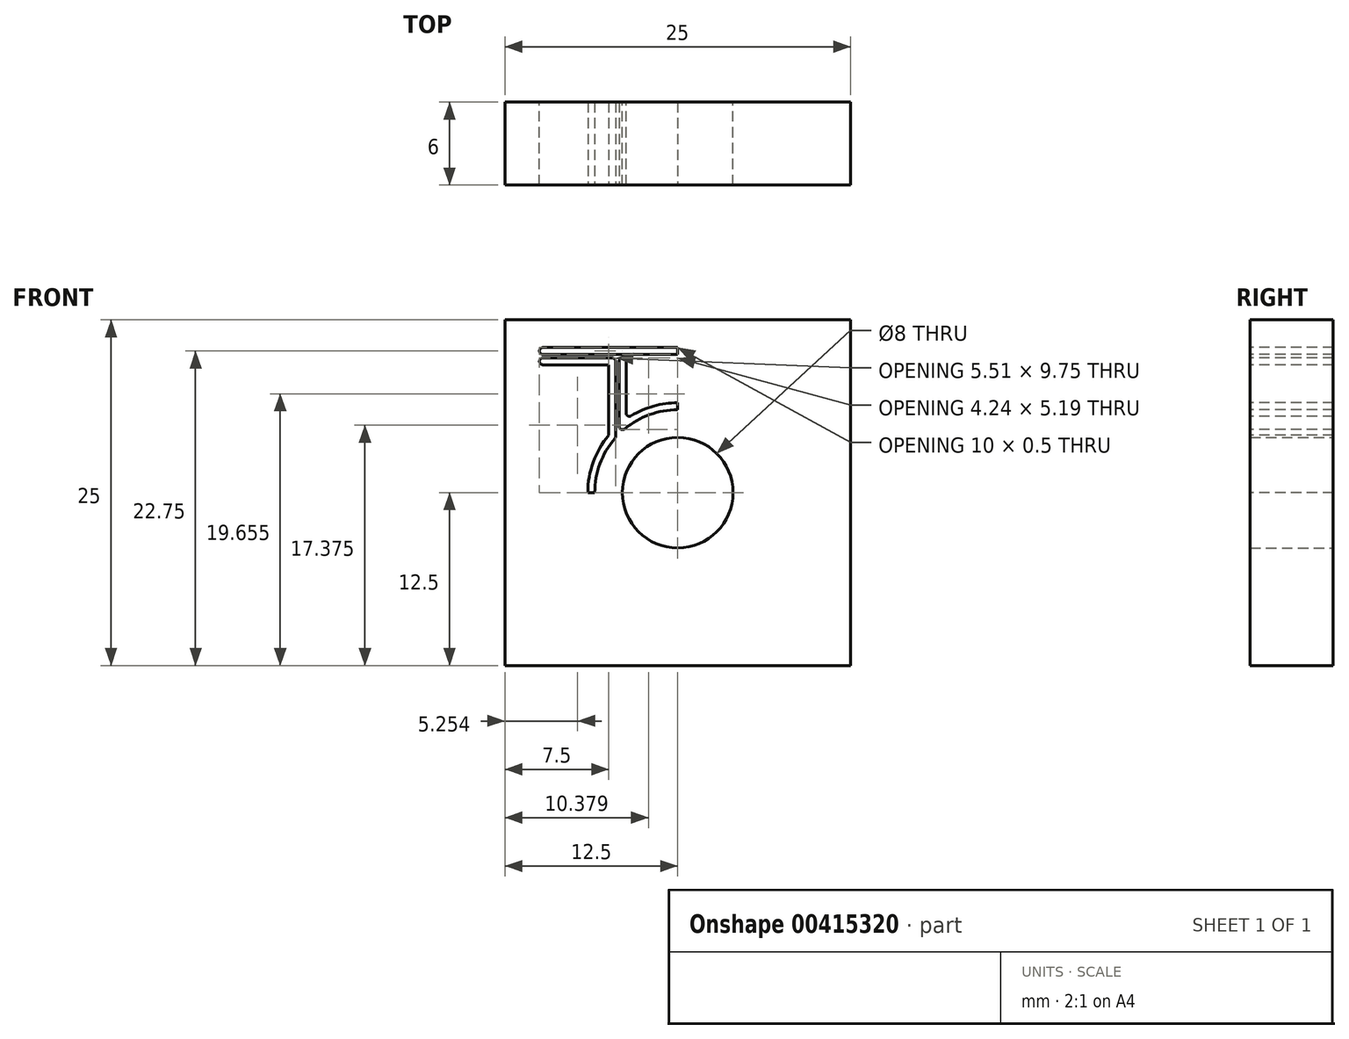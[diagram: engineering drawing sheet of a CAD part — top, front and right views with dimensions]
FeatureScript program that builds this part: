
annotation { "Feature Type Name" : "Feature", "Feature Type Description" : "" }
export const myFeature = defineFeature(function(context is Context, id is Id, definition is map)
    precondition{}
    {
        {
            var Q0;
            Q0=qCreatedBy(makeId("Front.planeOp"),FACE);
            var sketch = newSketch(context, id + "F0", { "sketchPlane" : qUnion([Q0])});
            skLineSegment(sketch, "E0.bottom", {"start": v(-12.5, 12.5) * mm, "end": v(12.5, 12.5) * mm});
            skLineSegment(sketch, "E0.top", {"start": v(-12.5, -12.5) * mm, "end": v(12.5, -12.5) * mm});
            skLineSegment(sketch, "E0.left", {"start": v(-12.5, 12.5) * mm, "end": v(-12.5, -12.5) * mm});
            skLineSegment(sketch, "E0.right", {"start": v(12.5, 12.5) * mm, "end": v(12.5, -12.5) * mm});
            skPoint(sketch, "E0.middle", {"position": v(0, 0) * mm});
            skCircle(sketch, "E1", {"center": v(0, 0) * mm, "radius": 4 * mm});
            skSolve(sketch);
        }
        {
            var Q0;
            Q0 = qSketchRegion(id + "F0", true);
            extrude(context, id + "F1", {"entities" : qUnion([Q0]), "flatOperationType" : FlatOperationType.REMOVE, "endBound" : BoundingType.SYMMETRIC, "offsetDistance" : 25 * mm, "depth" : 6 * mm, "domain" : OperationDomain.MODEL});
        }
        {
            var Q0;
            Q0=makeQuery(id+"F1.opExtrude","CAP_FACE",FACE,{"disambiguationData":[OSD([sQuery(id+"F0.wireOp",EDGE,"E0.bottom"),sQuery(id+"F0.wireOp",EDGE,"E0.top"),sQuery(id+"F0.wireOp",EDGE,"E0.left"),sQuery(id+"F0.wireOp",EDGE,"E0.right"),sQuery(id+"F0.wireOp",EDGE,"E1")])],"isStart":false});
            var sketch = newSketch(context, id + "F2", { "sketchPlane" : qUnion([Q0])});
            skCircle(sketch, "E2", {"center": v(0, 0) * mm, "radius": 6 * mm});
            skLineSegment(sketch, "E3", {"start": v(-4, 0) * mm, "end": v(4, 0) * mm, "construction": true});
            skLineSegment(sketch, "E4", {"start": v(0, 4) * mm, "end": v(0, -4) * mm, "construction": true});
            skLineSegment(sketch, "E5", {"start": v(-4.5, 3.98) * mm, "end": v(-4.5, 9.75) * mm});
            skLineSegment(sketch, "E6", {"start": v(-4.5, 9.75) * mm, "end": v(-10, 9.75) * mm});
            skLineSegment(sketch, "E7", {"start": v(-10, 9.75) * mm, "end": v(-10, 10) * mm});
            skLineSegment(sketch, "E8", {"start": v(-10, 10) * mm, "end": v(0, 10) * mm});
            skLineSegment(sketch, "E9", {"start": v(0, 10) * mm, "end": v(0, 9.75) * mm});
            skLineSegment(sketch, "E10", {"start": v(0, 9.75) * mm, "end": v(-4.24, 9.75) * mm});
            skLineSegment(sketch, "E11", {"start": v(-4.24, 9.75) * mm, "end": v(-4.24, 4.24) * mm});
            skLineSegment(sketch, "E12", {"start": v(-4.5, 9.75) * mm, "end": v(-4.24, 9.75) * mm, "construction": true});
            skLineSegment(sketch, "E13", {"start": v(0, 0) * mm, "end": v(-4.24, 4.24) * mm, "construction": true});
            skLineSegment(sketch, "E14", {"start": v(-10, 10) * mm, "end": v(-10, 10.5) * mm});
            skLineSegment(sketch, "E15", {"start": v(-10, 10.5) * mm, "end": v(0, 10.5) * mm});
            skLineSegment(sketch, "E16", {"start": v(0, 10.5) * mm, "end": v(0, 10) * mm});
            skLineSegment(sketch, "E17", {"start": v(-10, 9.75) * mm, "end": v(-10, 9.25) * mm});
            skLineSegment(sketch, "E18", {"start": v(-10, 9.25) * mm, "end": v(-5, 9.25) * mm});
            skLineSegment(sketch, "E19", {"start": v(-5, 9.25) * mm, "end": v(-5, 4.16) * mm});
            skLineSegment(sketch, "E20", {"start": v(-6, 0) * mm, "end": v(-6.5, 0) * mm});
            skArc(sketch, "E21", {"start": v(-5, 4.16) * mm, "mid": v(-6.11, 2.21) * mm, "end": v(-6.5, 0) * mm});
            skLineSegment(sketch, "E22", {"start": v(-5, 9.25) * mm, "end": v(-4.5, 9.25) * mm, "construction": true});
            skLineSegment(sketch, "E23", {"start": v(-3.74, 9.75) * mm, "end": v(-3.74, 5.31) * mm});
            skLineSegment(sketch, "E24", {"start": v(0, 6) * mm, "end": v(0, 6.5) * mm});
            skArc(sketch, "E25", {"start": v(0, 6.5) * mm, "mid": v(-1.96, 6.2) * mm, "end": v(-3.74, 5.31) * mm});
            skLineSegment(sketch, "E26", {"start": v(-4.24, 9.25) * mm, "end": v(-3.74, 9.25) * mm, "construction": true});
            skSolve(sketch);
        }
        {
            var Q0;
            {var subQ1=sQuery(id+"F2.wireOp",EDGE,"E5");Q0=makeQuery(id+"F2.imprint","IMPRINT",FACE,{"disambiguationData":[TD([[makeQuery(id+"F2.imprint","IMPRINT",EDGE,{"derivedFrom":subQ1}),1.0]])]});}
            var Q1;
            Q1=makeQuery(id+"F2.imprint","IMPRINT",FACE,{"disambiguationData":[TD([[makeQuery(id+"F2.imprint","IMPRINT",EDGE,{"derivedFrom":sQuery(id+"F2.wireOp",EDGE,"E10")}),1.0]])]});
            var Q2;
            Q2=makeQuery(id+"F2.imprint","IMPRINT",FACE,{"disambiguationData":[TD([[makeQuery(id+"F2.imprint","IMPRINT",EDGE,{"derivedFrom":sQuery(id+"F2.wireOp",EDGE,"E8")}),1.0]])]});
            extrude(context, id + "F3", {"entities" : qUnion([Q0, Q1, Q2]), "operationType" : NewBodyOperationType.REMOVE, "flatOperationType" : FlatOperationType.REMOVE, "endBound" : BoundingType.THROUGH_ALL, "oppositeDirection" : true, "offsetDistance" : 25 * mm, "depth" : 25 * mm, "domain" : OperationDomain.MODEL});
        }
        {
            var Q0;
            Q0=makeQuery(id+"F3.boolean.opBoolean","COPY",EDGE,{"derivedFrom":makeQuery(id+"F3.opExtrude","SWEPT_EDGE",EDGE,{"disambiguationData":[OSD([sQuery(id+"F2.wireOp",EDGE,"E7"),sQuery(id+"F2.wireOp",EDGE,"E8"),sQuery(id+"F2.wireOp",EDGE,"E14")])]})});
            var Q1;
            Q1=makeQuery(id+"F3.boolean.opBoolean","COPY",EDGE,{"derivedFrom":makeQuery(id+"F3.opExtrude","SWEPT_EDGE",EDGE,{"disambiguationData":[OSD([sQuery(id+"F2.wireOp",EDGE,"E5"),sQuery(id+"F2.wireOp",EDGE,"E6")])]})});
            var Q2;
            Q2=makeQuery(id+"F3.boolean.opBoolean","COPY",EDGE,{"derivedFrom":makeQuery(id+"F3.opExtrude","SWEPT_EDGE",EDGE,{"disambiguationData":[OSD([sQuery(id+"F2.wireOp",EDGE,"E2"),sQuery(id+"F2.wireOp",EDGE,"E5")])]})});
            var Q3;
            Q3=makeQuery(id+"F3.boolean.opBoolean","COPY",EDGE,{"derivedFrom":makeQuery(id+"F3.opExtrude","SWEPT_EDGE",EDGE,{"disambiguationData":[OSD([sQuery(id+"F2.wireOp",EDGE,"E2"),sQuery(id+"F2.wireOp",EDGE,"E11")])]})});
            var Q4;
            Q4=makeQuery(id+"Fz2yj0prLN2Bdhc_1.1.F3.boolean.opBoolean","COPY",EDGE,{"derivedFrom":makeQuery(id+"Fz2yj0prLN2Bdhc_1.1.F3.opExtrude","SWEPT_EDGE",EDGE,{"disambiguationData":[OSD([sQuery(id+"F2.wireOp",EDGE,"E2"),sQuery(id+"F2.wireOp",EDGE,"E11")])]})});
            var Q5;
            Q5=makeQuery(id+"Fz2yj0prLN2Bdhc_1.1.F3.boolean.opBoolean","COPY",EDGE,{"derivedFrom":makeQuery(id+"Fz2yj0prLN2Bdhc_1.1.F3.opExtrude","SWEPT_EDGE",EDGE,{"disambiguationData":[OSD([sQuery(id+"F2.wireOp",EDGE,"E5"),sQuery(id+"F2.wireOp",EDGE,"E6")])]})});
            var Q6;
            Q6=makeQuery(id+"Fz2yj0prLN2Bdhc_1.1.F3.boolean.opBoolean","COPY",EDGE,{"derivedFrom":makeQuery(id+"Fz2yj0prLN2Bdhc_1.1.F3.opExtrude","SWEPT_EDGE",EDGE,{"disambiguationData":[OSD([sQuery(id+"F2.wireOp",EDGE,"E2"),sQuery(id+"F2.wireOp",EDGE,"E5")])]})});
            var Q7;
            Q7=makeQuery(id+"Fz2yj0prLN2Bdhc_1.1.F3.boolean.opBoolean","COPY",EDGE,{"derivedFrom":makeQuery(id+"Fz2yj0prLN2Bdhc_1.1.F3.opExtrude","SWEPT_EDGE",EDGE,{"disambiguationData":[OSD([sQuery(id+"F2.wireOp",EDGE,"E6"),sQuery(id+"F2.wireOp",EDGE,"E7"),sQuery(id+"F2.wireOp",EDGE,"lAaYewaP-ejIx-ZsWI-JK7M-R26AU3mYNUki")])]})});
            var Q8;
            Q8=makeQuery(id+"Fz2yj0prLN2Bdhc_1.1.F3.boolean.opBoolean","COPY",EDGE,{"derivedFrom":makeQuery(id+"Fz2yj0prLN2Bdhc_1.1.F3.opExtrude","SWEPT_EDGE",EDGE,{"disambiguationData":[OSD([sQuery(id+"F2.wireOp",EDGE,"E14"),sQuery(id+"F2.wireOp",EDGE,"E15")])]})});
            var Q9;
            Q9=makeQuery(id+"F3.boolean.opBoolean","COPY",EDGE,{"derivedFrom":makeQuery(id+"F3.opExtrude","SWEPT_EDGE",EDGE,{"disambiguationData":[OSD([sQuery(id+"F2.wireOp",EDGE,"E14"),sQuery(id+"F2.wireOp",EDGE,"E15")])]})});
            var Q10;
            Q10=makeQuery(id+"Fz2yj0prLN2Bdhc_1.1.F3.boolean.opBoolean","COPY",EDGE,{"derivedFrom":makeQuery(id+"Fz2yj0prLN2Bdhc_1.1.F3.opExtrude","SWEPT_EDGE",EDGE,{"disambiguationData":[OSD([sQuery(id+"F2.wireOp",EDGE,"E7"),sQuery(id+"F2.wireOp",EDGE,"E8"),sQuery(id+"F2.wireOp",EDGE,"E14")])]})});
            var Q11;
            Q11=makeQuery(id+"Fz2yj0prLN2Bdhc_1.1.F3.boolean.opBoolean","COPY",EDGE,{"derivedFrom":makeQuery(id+"Fz2yj0prLN2Bdhc_1.1.F3.opExtrude","SWEPT_EDGE",EDGE,{"disambiguationData":[OSD([sQuery(id+"F2.wireOp",EDGE,"E10"),sQuery(id+"F2.wireOp",EDGE,"E11")])]})});
            var Q12;
            Q12=makeQuery(id+"F3.boolean.opBoolean","COPY",EDGE,{"derivedFrom":makeQuery(id+"F3.opExtrude","SWEPT_EDGE",EDGE,{"disambiguationData":[OSD([sQuery(id+"F2.wireOp",EDGE,"E10"),sQuery(id+"F2.wireOp",EDGE,"E11")])]})});
            var Q13;
            Q13=makeQuery(id+"F3.boolean.opBoolean","COPY",EDGE,{"derivedFrom":makeQuery(id+"F3.opExtrude","SWEPT_EDGE",EDGE,{"disambiguationData":[OSD([sQuery(id+"F2.wireOp",EDGE,"E17"),sQuery(id+"F2.wireOp",EDGE,"E18")])]})});
            var Q14;
            Q14=makeQuery(id+"F3.boolean.opBoolean","COPY",EDGE,{"derivedFrom":makeQuery(id+"F3.opExtrude","SWEPT_EDGE",EDGE,{"disambiguationData":[OSD([sQuery(id+"F2.wireOp",EDGE,"E6"),sQuery(id+"F2.wireOp",EDGE,"E7"),sQuery(id+"F2.wireOp",EDGE,"E17")])]})});
            var Q15;
            Q15=makeQuery(id+"F3.boolean.opBoolean","COPY",EDGE,{"derivedFrom":makeQuery(id+"F3.opExtrude","SWEPT_EDGE",EDGE,{"disambiguationData":[OSD([sQuery(id+"F2.wireOp",EDGE,"E10"),sQuery(id+"F2.wireOp",EDGE,"E23")])]})});
            var Q16;
            Q16=makeQuery(id+"F3.boolean.opBoolean","COPY",EDGE,{"derivedFrom":makeQuery(id+"F3.opExtrude","SWEPT_EDGE",EDGE,{"disambiguationData":[OSD([sQuery(id+"F2.wireOp",EDGE,"E23"),sQuery(id+"F2.wireOp",EDGE,"E25")])]})});
            fillet(context, id + "F4", {"entities" : qUnion([Q0, Q1, Q2, Q3, Q4, Q5, Q6, Q7, Q8, Q9, Q10, Q11, Q12, Q13, Q14, Q15, Q16]), "radius" : .25 * mm, "tangentPropagation" : true, "defaultsChanged" : false, "vertexSettings" : [], "allowEdgeOverflow" : false});
        }
    });
